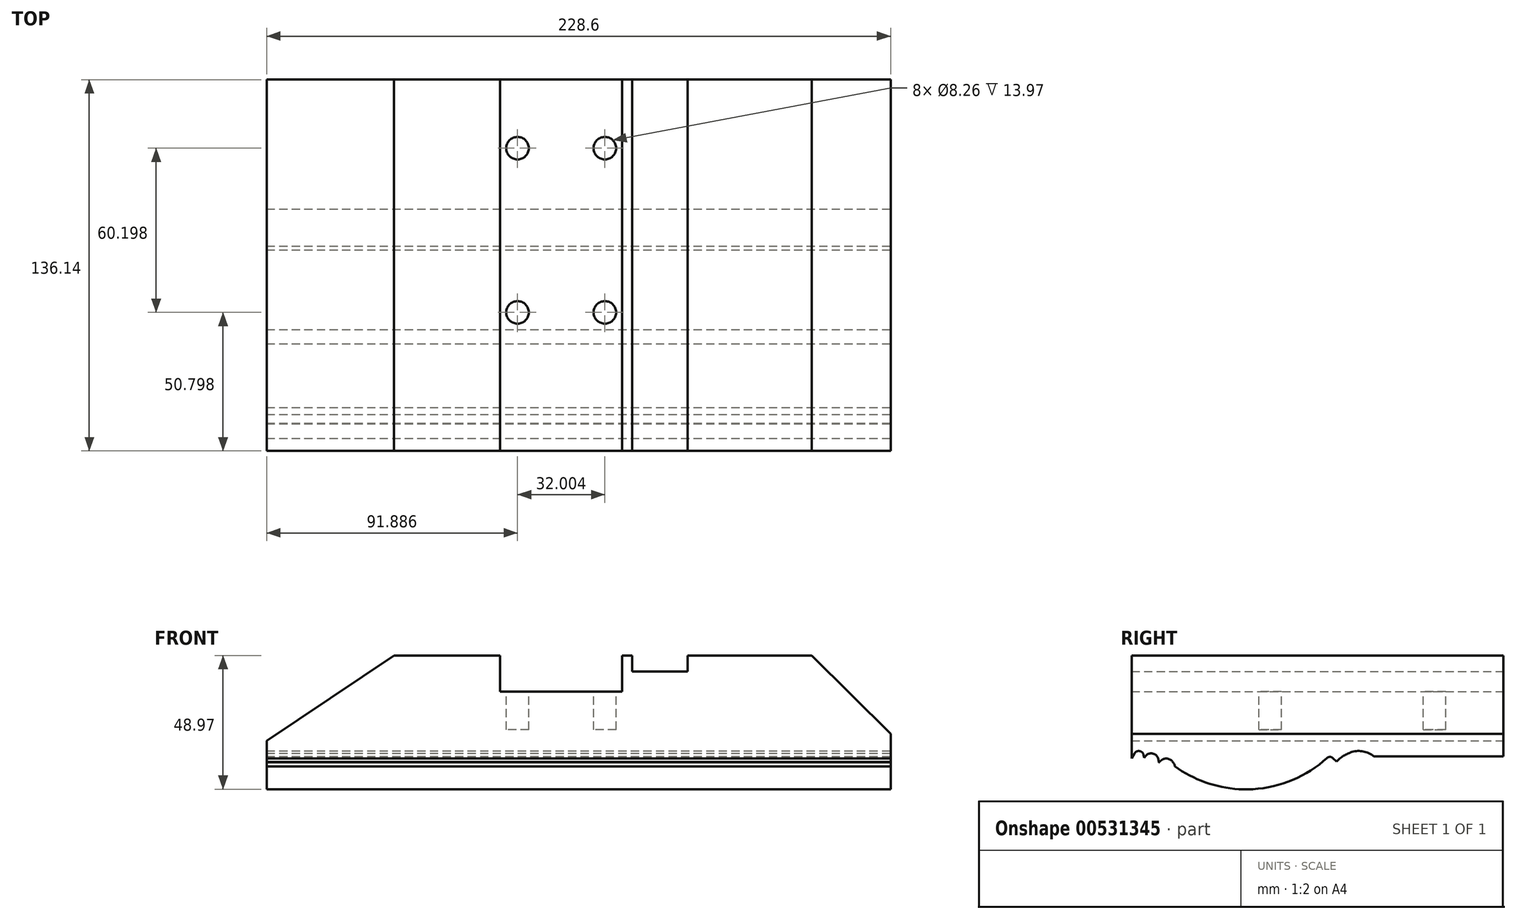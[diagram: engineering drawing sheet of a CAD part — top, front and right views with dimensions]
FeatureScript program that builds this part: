
annotation { "Feature Type Name" : "Feature", "Feature Type Description" : "" }
export const myFeature = defineFeature(function(context is Context, id is Id, definition is map)
    precondition{}
    {
        {
            var Q0;
            Q0=qCreatedBy(makeId("Front.planeOp"),FACE);
            var sketch = newSketch(context, id + "F0", { "sketchPlane" : qUnion([Q0])});
            skLineSegment(sketch, "E0", {"start": v(0, 0) * mm, "end": v(114.3, 0) * mm});
            skLineSegment(sketch, "E1", {"start": v(0, 0) * mm, "end": v(-114.3, 0) * mm});
            skLineSegment(sketch, "E2", {"start": v(-114.3, 0) * mm, "end": v(-114.3, 17.78) * mm});
            skLineSegment(sketch, "E3", {"start": v(-67.63, 48.97) * mm, "end": v(-28.76, 48.97) * mm});
            skLineSegment(sketch, "E4", {"start": v(114.3, 20.32) * mm, "end": v(114.3, 0) * mm});
            skPoint(sketch, "E5", {"position": v(-114.3, 0) * mm});
            skPoint(sketch, "E6", {"position": v(-114.3, 17.78) * mm});
            skPoint(sketch, "E7", {"position": v(114.3, 20.32) * mm});
            skLineSegment(sketch, "E8", {"start": v(-114.3, 17.78) * mm, "end": v(-67.63, 48.97) * mm});
            skPoint(sketch, "E9", {"position": v(-28.76, 48.97) * mm});
            skLineSegment(sketch, "E10", {"start": v(-28.76, 48.97) * mm, "end": v(-28.76, 35.76) * mm});
            skLineSegment(sketch, "E11", {"start": v(-28.76, 35.76) * mm, "end": v(15.94, 35.76) * mm});
            skLineSegment(sketch, "E12", {"start": v(15.94, 35.76) * mm, "end": v(15.94, 48.97) * mm});
            skLineSegment(sketch, "E13.trimOffspring", {"start": v(15.94, 48.97) * mm, "end": v(19.57, 48.97) * mm});
            skLineSegment(sketch, "E14", {"start": v(19.57, 48.97) * mm, "end": v(19.57, 43.12) * mm});
            skLineSegment(sketch, "E15", {"start": v(19.57, 43.12) * mm, "end": v(39.9, 43.12) * mm});
            skLineSegment(sketch, "E16", {"start": v(39.9, 43.12) * mm, "end": v(39.9, 48.97) * mm});
            skLineSegment(sketch, "E17.trimOffspring", {"start": v(39.9, 48.97) * mm, "end": v(85.36, 48.97) * mm});
            skPoint(sketch, "E18", {"position": v(85.36, 48.97) * mm});
            skLineSegment(sketch, "E19", {"start": v(85.36, 48.97) * mm, "end": v(114.3, 20.32) * mm});
            skSolve(sketch);
        }
        {
            var Q0;
            Q0 = qSketchRegion(id + "F0", true);
            var Q1;
            Q1 = qSketchRegion(id + "F2", true);
            extrude(context, id + "F1", {"entities" : qUnion([Q0, Q1]), "depth" : 68.07 * mm, "offsetDistance" : 25.4 * mm, "hasSecondDirection" : true, "secondDirectionOppositeDirection" : true, "secondDirectionDepth" : 68.07 * mm});
        }
        {
            var Q0;
            Q0=makeQuery(id+"F1.opExtrude","SWEPT_FACE",FACE,{"disambiguationData":[OSD([sQuery(id+"F0.wireOp",EDGE,"E11")])]});
            var sketch = newSketch(context, id + "F2", { "sketchPlane" : qUnion([Q0])});
            skCircle(sketch, "E20", {"center": v(-22.41, -17.27) * mm, "radius": 4.13 * mm});
            skCircle(sketch, "E21", {"center": v(9.6, -17.27) * mm, "radius": 4.13 * mm});
            skCircle(sketch, "E22", {"center": v(-22.41, 42.93) * mm, "radius": 4.13 * mm});
            skCircle(sketch, "E23", {"center": v(9.6, 42.93) * mm, "radius": 4.13 * mm});
            skSolve(sketch);
        }
        {
            var Q0;
            Q0=makeQuery(id+"F2.imprint","IMPRINT",FACE,{"disambiguationData":[TD([[makeQuery(id+"F2.imprint","IMPRINT",EDGE,{"derivedFrom":sQuery(id+"F2.wireOp",EDGE,"E22")}),1.0]])]});
            var Q1;
            Q1=makeQuery(id+"F2.imprint","IMPRINT",FACE,{"disambiguationData":[TD([[makeQuery(id+"F2.imprint","IMPRINT",EDGE,{"derivedFrom":sQuery(id+"F2.wireOp",EDGE,"E23")}),1.0]])]});
            var Q2;
            Q2=makeQuery(id+"F2.imprint","IMPRINT",FACE,{"disambiguationData":[TD([[makeQuery(id+"F2.imprint","IMPRINT",EDGE,{"derivedFrom":sQuery(id+"F2.wireOp",EDGE,"E21")}),1.0]])]});
            var Q3;
            Q3=makeQuery(id+"F2.imprint","IMPRINT",FACE,{"disambiguationData":[TD([[makeQuery(id+"F2.imprint","IMPRINT",EDGE,{"derivedFrom":sQuery(id+"F2.wireOp",EDGE,"E20")}),1.0]])]});
            extrude(context, id + "F3", {"entities" : qUnion([Q0, Q1, Q2, Q3]), "operationType" : NewBodyOperationType.REMOVE, "oppositeDirection" : true, "depth" : 13.97 * mm, "offsetDistance" : 25.4 * mm});
        }
        {
            var Q0;
            Q0=makeQuery(id+"F1.opExtrude","SWEPT_FACE",FACE,{"disambiguationData":[OSD([sQuery(id+"F0.wireOp",EDGE,"E4")])]});
            var sketch = newSketch(context, id + "F4", { "sketchPlane" : qUnion([Q0])});
            skPoint(sketch, "E24.endSnap0", {"position": v(0, 20.32) * mm});
            skPoint(sketch, "E25", {"position": v(-23.62, 14) * mm});
            skPoint(sketch, "E26", {"position": v(-52.2, 14) * mm});
            skPoint(sketch, "E27", {"position": v(-52.2, 8.38) * mm});
            skPoint(sketch, "E28", {"position": v(20.83, 14) * mm});
            skPoint(sketch, "E29", {"position": v(3.53, 14) * mm});
            skPoint(sketch, "E30", {"position": v(3.53, 11.43) * mm});
            skArc(sketch, "E31", {"start": v(-52.2, 8.38) * mm, "mid": v(-23.8, 0) * mm, "end": v(3.53, 11.43) * mm});
            skPoint(sketch, "E32", {"position": v(5.66, 11.43) * mm});
            skArc(sketch, "E33", {"start": v(5.66, 11.43) * mm, "mid": v(4.6, 11.85) * mm, "end": v(3.53, 11.43) * mm});
            skLineSegment(sketch, "E34", {"start": v(5.66, 11.43) * mm, "end": v(6.98, 10.06) * mm});
            skArc(sketch, "E35", {"start": v(12.67, 13.61) * mm, "mid": v(9.6, 12.21) * mm, "end": v(6.98, 10.06) * mm});
            skArc(sketch, "E36", {"start": v(20.68, 12.07) * mm, "mid": v(16.87, 13.84) * mm, "end": v(12.67, 13.61) * mm});
            skArc(sketch, "E37", {"start": v(-58.16, 10.03) * mm, "mid": v(-58.05, 9.87) * mm, "end": v(-57.86, 9.93) * mm});
            skArc(sketch, "E38", {"start": v(-56.5, 11) * mm, "mid": v(-57.24, 10.54) * mm, "end": v(-57.86, 9.93) * mm});
            skArc(sketch, "E39", {"start": v(-54.7, 11.13) * mm, "mid": v(-55.6, 11.23) * mm, "end": v(-56.5, 11) * mm});
            skArc(sketch, "E40", {"start": v(-52.2, 8.38) * mm, "mid": v(-53.06, 10.1) * mm, "end": v(-54.7, 11.13) * mm});
            skLineSegment(sketch, "E41", {"start": v(-58.27, 10.82) * mm, "end": v(-58.16, 10.03) * mm});
            skArc(sketch, "E42", {"start": v(-58.27, 10.82) * mm, "mid": v(-60.2, 13.02) * mm, "end": v(-63, 12.12) * mm});
            skLineSegment(sketch, "E43", {"start": v(-63, 12.12) * mm, "end": v(-63.48, 11.52) * mm});
            skLineSegment(sketch, "E44", {"start": v(-63.67, 12.53) * mm, "end": v(-63.48, 11.52) * mm});
            skArc(sketch, "E45", {"start": v(-63.67, 12.53) * mm, "mid": v(-65.14, 13.96) * mm, "end": v(-67, 13.09) * mm});
            skLineSegment(sketch, "E46", {"start": v(-67, 13.09) * mm, "end": v(-68.07, 11.27) * mm});
            skPoint(sketch, "E47.start.orphan", {"position": v(-68.07, 14) * mm});
            skPoint(sketch, "E48.end.orphan", {"position": v(-23.62, 0) * mm});
            skLineSegment(sketch, "E49.trimOffspring", {"start": v(15.03, 14) * mm, "end": v(15.41, 14) * mm, "construction": true});
            skPoint(sketch, "E50.orphan", {"position": v(0, 0) * mm});
            skPoint(sketch, "E24.end.orphan", {"position": v(0, 14) * mm});
            skPoint(sketch, "E51.end.orphan", {"position": v(20.68, 0) * mm});
            skLineSegment(sketch, "E52", {"start": v(20.68, 12.07) * mm, "end": v(68.07, 12.07) * mm});
            skSolve(sketch);
        }
        {
            var Q0;
            Q0=makeQuery(id+"F4.imprint","IMPRINT",FACE,{"disambiguationData":[TD([[makeQuery(id+"F4.imprint","IMPRINT",EDGE,{"derivedFrom":sQuery(id+"F4.wireOp",EDGE,"E37")}),-1.0]])]});
            extrude(context, id + "F5", {"entities" : qUnion([Q0]), "operationType" : NewBodyOperationType.REMOVE, "oppositeDirection" : true, "depth" : 228.6 * mm, "offsetDistance" : 25.4 * mm});
        }
        {
            var Q0;
            {var subQ0=sQuery(id+"F4.wireOp",EDGE,"E33");Q0=makeQuery(id+"F4.imprint","IMPRINT",FACE,{"disambiguationData":[TD([[makeQuery(id+"F4.imprint","IMPRINT",EDGE,{"derivedFrom":subQ0}),1.0]])]});}
            extrude(context, id + "F6", {"entities" : qUnion([Q0]), "operationType" : NewBodyOperationType.REMOVE, "oppositeDirection" : true, "depth" : 228.6 * mm, "offsetDistance" : 25.4 * mm});
        }
    });
